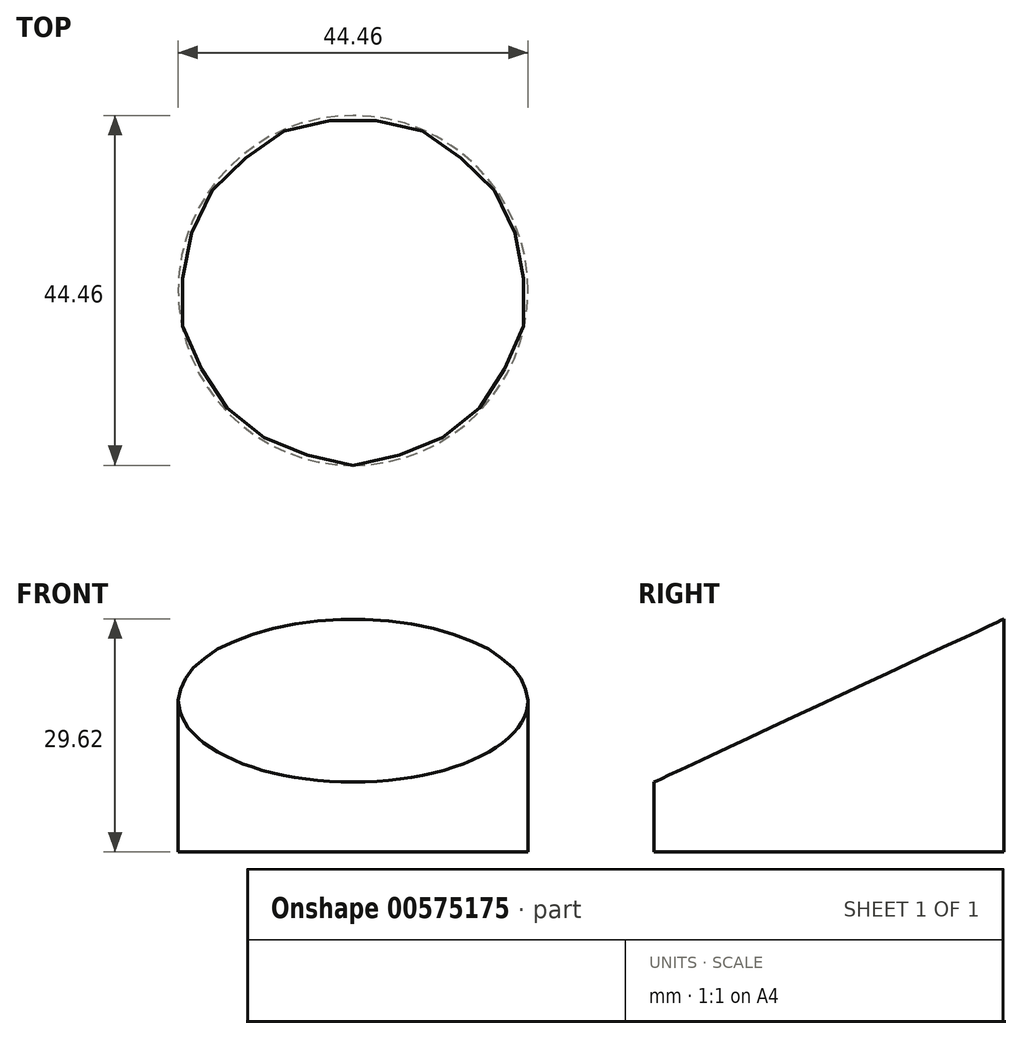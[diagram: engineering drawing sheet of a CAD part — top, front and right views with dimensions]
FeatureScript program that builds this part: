
annotation { "Feature Type Name" : "Feature", "Feature Type Description" : "" }
export const myFeature = defineFeature(function(context is Context, id is Id, definition is map)
    precondition{}
    {
        {
            var Q0;
            Q0=qCreatedBy(makeId("Top.planeOp"),FACE);
            var sketch = newSketch(context, id + "F0", { "sketchPlane" : qUnion([Q0])});
            skCircle(sketch, "E0", {"center": v(0, 0) * mm, "radius": 22.23 * mm});
            skSolve(sketch);
        }
        {
            var Q0;
            Q0 = qSketchRegion(id + "F0", true);
            extrude(context, id + "F1", {"entities" : qUnion([Q0]), "depth" : 38.1 * mm, "offsetDistance" : 25.4 * mm});
        }
        {
            var Q0;
            Q0=qCreatedBy(makeId("Right.planeOp"),FACE);
            var sketch = newSketch(context, id + "F2", { "sketchPlane" : qUnion([Q0])});
            skLineSegment(sketch, "E1", {"start": v(-22.23, 8.9) * mm, "end": v(64.35, 49.26) * mm});
            skLineSegment(sketch, "E2", {"start": v(-22.23, 38.1) * mm, "end": v(-22.23, 0) * mm, "construction": true});
            skLineSegment(sketch, "E3", {"start": v(64.35, 49.26) * mm, "end": v(-22.23, 49.26) * mm});
            skLineSegment(sketch, "E4", {"start": v(-22.23, 49.26) * mm, "end": v(-22.23, 8.9) * mm});
            skSolve(sketch);
        }
        {
            var Q0;
            Q0 = qSketchRegion(id + "F2", true);
            extrude(context, id + "F3", {"entities" : qUnion([Q0]), "operationType" : NewBodyOperationType.REMOVE, "endBound" : BoundingType.THROUGH_ALL, "oppositeDirection" : true, "depth" : 25.4 * mm, "offsetDistance" : 25.4 * mm, "hasSecondDirection" : true, "secondDirectionBound" : SecondDirectionBoundingType.THROUGH_ALL, "secondDirectionOppositeDirection" : false, "secondDirectionDepth" : 25.4 * mm});
        }
    });
